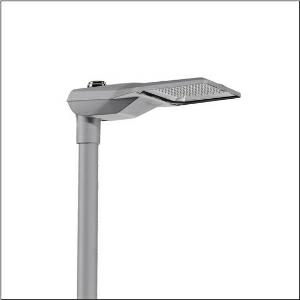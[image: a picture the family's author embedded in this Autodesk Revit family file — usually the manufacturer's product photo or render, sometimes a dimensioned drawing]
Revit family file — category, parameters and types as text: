
# Revit family: streetlight_sl_21_midi___st0_8a_5xe7c47n08mb_cd2e
name_source: partatom
category: Lighting Fixtures
units: mm (PartAtom-declared; Revit-internal decimal feet)

## family parameters
Cut with Voids When Loaded = No
Host = Face
Light Source = No
Part Type = Normal
Room Calculation Point = No
Round Connector Dimension = Use Diameter
Shared = No

## types (1)
- --- (1 x LED, 20180 lm, 147 W, 4000K)
    Apparent Load = 147 VA
    CIE Flux Codes = 38 75 97 100 100
    Color Rendering = 70
    Color Temperature = 4000K
    Default Elevation = 1800 mm
    Description = Streetlight SL 21 midi, mast luminaire, primary light control with lens, of PMMA, primary optical cover: cover, of toughened safety glass, transparent, light distribution: ST0.8a, light emission: direct distribution, primary light characteristic: asymmetric, installation type: side-entry, LED, 3G 2.5mm², High Power LED, rated luminous flux: 20.180lm, luminous efficacy: 137lm/W, light colour: 740, colour temperature: 4000K, control gear: NEMA (7pin), control: overheat protection, pre-setting: linear dimming characteristic, constant luminous flux control, time-dependent luminous flux control, flexible luminous flux parameterisation, mains connection: 220..240V, AC, 50/60Hz, connection cable pre-assembled, cable length: 12,5m, wiring characteristics: H05VV-F, start of lifetime: 147W, end of service life: 155W, reduction: 65W, luminaire housing, of diecast aluminium (EN AC-44300), powder-coated, SITECO metallic grey (DB 702S), corrosivity category C5 high according to DIN EN ISO 12944, multi-level sealing system, sealing non-destructively replaceable, inclination adjustable: 0°, 5°, 10°, 15°, length: 644mm, width: 335mm, height: 110mm, spigot size: 42mm (side-entry), mounting height: 4..8m, protection rating (complete): IP66, insulation class (complete): insulation class I (protective earthing), certification: CE, ENEC, ENEC+, VDE, impact resistance: IK10, permissible operating ambient temperature for outdoor applications: -40..+50°C, standard-compliant lighting for roads and squares, packaging unit: 1 piece

Light Distribution: ST0.8a
    Height = 111 mm
    Lamp = 1 x LED
    Lamp Light Flux = 20180 lm
    Lamp Power = 147 W
    Lamp count = 1
    Length = 644 mm
    Luminous efficacy = 137 lm/W
    Manufacturer = Siteco
    ModVariant = No
    Model = 5XE7C47N08MB
    Number of Poles = 1
    OnlyDefault = Yes
    Power Factor = 1
    Product Name = Streetlight SL 21 midi | ST0.8a
    Product group = mast luminaire | pylon top
    ProductGroupID = 6100
    Protection Class = Protection class I
    Protection Degree = IP 66
    RLX_Detail_Level = 1
    RLX_Emergency_Light_Flux = 0 lm
    RLX_Emergency_Type = 0
    RLX_Emergency_Type_DB = No
    RlxData = <blob elided: 26629 chars, md5=208b2b9c>
    Socket = socket
    Standby Power = 0 W
    System Light Flux = 20180 lm
    System Power = 147 W
    Type Comments = factory setting: luminous flux: 100 % | dim-lin: 254 | 750 mA
    Type Image = l_1294377.jpg
    URL = http://relux.com
    VarID = @adj_133487
    Voltage = 0 V
    Weight = 0.00 kg
    Width = 336 mm

## geometry (parser evidence)
native form markers: Blend x4, Sweep x11
no freeform markers — native parametric forms only
